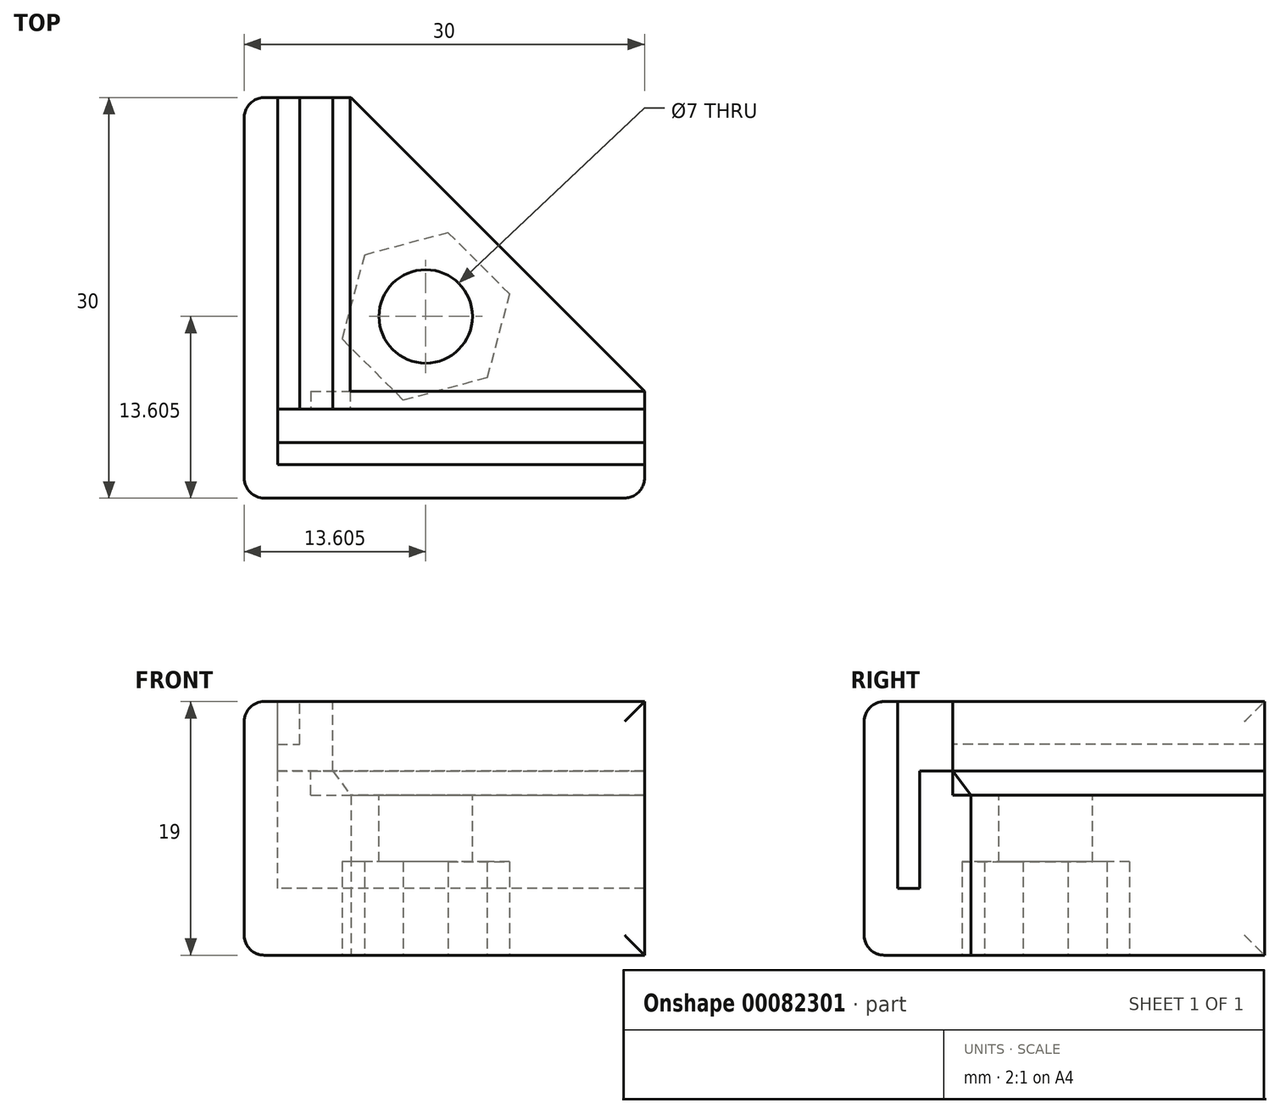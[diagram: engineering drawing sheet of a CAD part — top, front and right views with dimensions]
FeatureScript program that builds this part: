
annotation { "Feature Type Name" : "Feature", "Feature Type Description" : "" }
export const myFeature = defineFeature(function(context is Context, id is Id, definition is map)
    precondition{}
    {
        {
            var Q0;
            Q0=qCreatedBy(makeId("Top.planeOp"),FACE);
            var sketch = newSketch(context, id + "F0", { "sketchPlane" : qUnion([Q0])});
            skLineSegment(sketch, "E0", {"start": v(0, 0) * mm, "end": v(0, 30) * mm});
            skLineSegment(sketch, "E1", {"start": v(0, 30) * mm, "end": v(8, 30) * mm});
            skLineSegment(sketch, "E2", {"start": v(8, 30) * mm, "end": v(30, 8) * mm});
            skLineSegment(sketch, "E3", {"start": v(30, 8) * mm, "end": v(30, 0) * mm});
            skLineSegment(sketch, "E4", {"start": v(30, 0) * mm, "end": v(0, 0) * mm});
            skSolve(sketch);
        }
        {
            var Q0;
            Q0=makeQuery(id+"F0.imprint","IMPRINT",FACE,{"disambiguationData":[TD([[makeQuery(id+"F0.imprint","IMPRINT",EDGE,{"derivedFrom":sQuery(id+"F0.wireOp",EDGE,"E0")}),-1.0]])]});
            extrude(context, id + "F1", {"entities" : qUnion([Q0]), "depth" : 19 * mm});
        }
        {
            var Q0;
            Q0=makeQuery(id+"F1.opExtrude","CAP_FACE",FACE,{"disambiguationData":[OSD([sQuery(id+"F0.wireOp",EDGE,"E0"),sQuery(id+"F0.wireOp",EDGE,"E1"),sQuery(id+"F0.wireOp",EDGE,"E2"),sQuery(id+"F0.wireOp",EDGE,"E3"),sQuery(id+"F0.wireOp",EDGE,"E4")])],"isStart":false});
            var sketch = newSketch(context, id + "F2", { "sketchPlane" : qUnion([Q0])});
            skLineSegment(sketch, "E5", {"start": v(2.5, 30) * mm, "end": v(2.5, 4.15) * mm});
            skLineSegment(sketch, "E6", {"start": v(2.5, 4.15) * mm, "end": v(4.15, 4.15) * mm});
            skLineSegment(sketch, "E7", {"start": v(4.15, 6.65) * mm, "end": v(4.15, 30) * mm});
            skLineSegment(sketch, "E8", {"start": v(4.15, 30) * mm, "end": v(2.5, 30) * mm});
            skLineSegment(sketch, "E9", {"start": v(30, 2.5) * mm, "end": v(2.5, 2.5) * mm});
            skLineSegment(sketch, "E10", {"start": v(2.5, 2.5) * mm, "end": v(2.5, 4.15) * mm});
            skLineSegment(sketch, "E11", {"start": v(2.5, 4.15) * mm, "end": v(30, 4.15) * mm});
            skLineSegment(sketch, "E12", {"start": v(30, 4.15) * mm, "end": v(30, 2.5) * mm});
            skLineSegment(sketch, "E13", {"start": v(30, 6.65) * mm, "end": v(2.5, 6.65) * mm});
            skLineSegment(sketch, "E14", {"start": v(6.65, 30) * mm, "end": v(6.65, 6.65) * mm});
            skCircle(sketch, "E15", {"center": v(13.6, 13.6) * mm, "radius": 3.5 * mm});
            skSolve(sketch);
        }
        {
            var Q0;
            Q0=makeQuery(id+"F2.imprint","IMPRINT",FACE,{"disambiguationData":[TD([[makeQuery(id+"F2.imprint","IMPRINT",EDGE,{"derivedFrom":sQuery(id+"F2.wireOp",EDGE,"E9")}),-1.0]])]});
            extrude(context, id + "F3", {"entities" : qUnion([Q0]), "operationType" : NewBodyOperationType.REMOVE, "oppositeDirection" : true, "depth" : 14 * mm});
        }
        {
            var Q0;
            {var subQ5=sQuery(id+"F2.wireOp",EDGE,"E5");Q0=makeQuery(id+"F2.imprint","IMPRINT",FACE,{"disambiguationData":[TD([[makeQuery(id+"F2.imprint","IMPRINT",EDGE,{"derivedFrom":subQ5}),1.0]])]});}
            extrude(context, id + "F4", {"entities" : qUnion([Q0]), "operationType" : NewBodyOperationType.REMOVE, "oppositeDirection" : true, "depth" : 3.2 * mm});
        }
        {
            var Q0;
            {var subQ0=sQuery(id+"F2.wireOp",EDGE,"E11");var subQ3=makeQuery(id+"F2.imprint","IMPRINT",VERTEX,{"derivedFrom":subQ0});Q0=makeQuery(id+"F2.imprint","IMPRINT",FACE,{"disambiguationData":[TD([[makeQuery(id+"F2.imprint","IMPRINT",EDGE,{"disambiguationData":[TD([[subQ3,1.0]])],"derivedFrom":subQ0}),1.0]])]});}
            extrude(context, id + "F5", {"entities" : qUnion([Q0]), "operationType" : NewBodyOperationType.REMOVE, "oppositeDirection" : true, "depth" : 5.2 * mm});
        }
        {
            var Q0;
            {var subQ2=sQuery(id+"F2.wireOp",EDGE,"E14");Q0=makeQuery(id+"F2.imprint","IMPRINT",FACE,{"disambiguationData":[TD([[makeQuery(id+"F2.imprint","IMPRINT",EDGE,{"derivedFrom":subQ2}),1.0]])]});}
            extrude(context, id + "F6", {"entities" : qUnion([Q0]), "operationType" : NewBodyOperationType.REMOVE, "oppositeDirection" : true, "depth" : 7 * mm});
        }
        {
            var Q0;
            Q0=makeQuery(id+"F0.imprint","IMPRINT",FACE,{"disambiguationData":[TD([[makeQuery(id+"F0.imprint","IMPRINT",EDGE,{"derivedFrom":sQuery(id+"F0.wireOp",EDGE,"E0")}),-1.0]])]});
            var sketch = newSketch(context, id + "F7", { "sketchPlane" : qUnion([Q0])});
            skLineSegment(sketch, "E16", {"start": v(15.29, 19.88) * mm, "end": v(19.88, 15.29) * mm});
            skLineSegment(sketch, "E17", {"start": v(15.29, 19.88) * mm, "end": v(9, 18.2) * mm});
            skLineSegment(sketch, "E18", {"start": v(9, 18.2) * mm, "end": v(7.33, 11.92) * mm});
            skLineSegment(sketch, "E19", {"start": v(19.88, 15.29) * mm, "end": v(18.2, 9) * mm});
            skLineSegment(sketch, "E20", {"start": v(18.2, 9) * mm, "end": v(11.92, 7.33) * mm});
            skLineSegment(sketch, "E21", {"start": v(11.92, 7.33) * mm, "end": v(7.33, 11.92) * mm});
            skCircle(sketch, "E22", {"center": v(13.6, 13.6) * mm, "radius": 3.5 * mm});
            skSolve(sketch);
        }
        {
            var Q0;
            Q0=makeQuery(id+"F7.imprint","IMPRINT",FACE,{"disambiguationData":[TD([[makeQuery(id+"F7.imprint","IMPRINT",EDGE,{"derivedFrom":sQuery(id+"F7.wireOp",EDGE,"E16")}),-1.0]])]});
            extrude(context, id + "F8", {"entities" : qUnion([Q0]), "operationType" : NewBodyOperationType.REMOVE, "depth" : 7 * mm});
        }
        {
            var Q0;
            Q0=makeQuery(id+"F2.imprint","IMPRINT",FACE,{"disambiguationData":[TD([[makeQuery(id+"F2.imprint","IMPRINT",EDGE,{"derivedFrom":sQuery(id+"F2.wireOp",EDGE,"E15")}),1.0]])]});
            extrude(context, id + "F9", {"entities" : qUnion([Q0]), "operationType" : NewBodyOperationType.REMOVE, "oppositeDirection" : true, "depth" : 25 * mm});
        }
        {
            var Q0;
            Q0=makeQuery(id+"F1.opExtrude","SWEPT_FACE",FACE,{"disambiguationData":[OSD([sQuery(id+"F0.wireOp",EDGE,"E4")])]});
            var Q1;
            Q1=makeQuery(id+"F1.opExtrude","SWEPT_FACE",FACE,{"disambiguationData":[OSD([sQuery(id+"F0.wireOp",EDGE,"E0")])]});
            fillet(context, id + "F10", {"entities" : qUnion([Q0, Q1]), "radius" : 1.5 * mm, "tangentPropagation" : true, "allowEdgeOverflow" : false});
        }
        {
            var Q0;
            Q0=makeQuery(id+"F6.boolean.opBoolean","COPY",FACE,{"derivedFrom":makeQuery(id+"F6.opExtrude","SWEPT_FACE",FACE,{"disambiguationData":[OSD([sQuery(id+"F2.wireOp",EDGE,"E13")])]})});
            var sketch = newSketch(context, id + "F11", { "sketchPlane" : qUnion([Q0])});
            skLineSegment(sketch, "E23", {"start": v(-6.65, 13.8) * mm, "end": v(-7.95, 12) * mm});
            skSolve(sketch);
        }
        {
            var Q0;
            {var subQ0=sQuery(id+"F11.wireOp",EDGE,"E23");Q0=makeQuery(id+"F11.imprint","IMPRINT",FACE,{"disambiguationData":[TD([[makeQuery(id+"F11.imprint","IMPRINT",EDGE,{"derivedFrom":subQ0}),1.0]])]});}
            extrude(context, id + "F12", {"entities" : qUnion([Q0]), "operationType" : NewBodyOperationType.ADD, "depth" : 23.35 * mm});
        }
        {
            var Q0;
            Q0=makeQuery(id+"F1.opExtrude","SWEPT_FACE",FACE,{"disambiguationData":[OSD([sQuery(id+"F0.wireOp",EDGE,"E3")])]});
            var sketch = newSketch(context, id + "F13", { "sketchPlane" : qUnion([Q0])});
            skLineSegment(sketch, "E24", {"start": v(8, 12) * mm, "end": v(6.65, 13.8) * mm});
            skSolve(sketch);
        }
        {
            var Q0;
            Q0=makeQuery(id+"F13.imprint","IMPRINT",FACE,{"disambiguationData":[TD([[makeQuery(id+"F13.imprint","IMPRINT",EDGE,{"derivedFrom":sQuery(id+"F13.wireOp",EDGE,"E24")}),1.0]])]});
            extrude(context, id + "F14", {"entities" : qUnion([Q0]), "oppositeDirection" : true, "depth" : 25 * mm});
        }
    });
